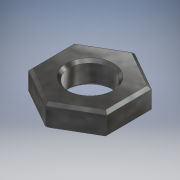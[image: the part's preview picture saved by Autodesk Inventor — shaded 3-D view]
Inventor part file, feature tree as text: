
AUTODESK INVENTOR PART (.ipt)
format: ipt  version: 2017 (Build 210142000, 142)  size: 131,072 bytes
history: native  units: mm
features: extrude x1, chamfer x1, sketch x1
ambient origin geometry x8: Origin, YZ Plane, XZ Plane, XY Plane, X Axis, Y Axis, Z Axis, Center Point
bodies: Solid1 (feature_tree)
feature tree (3):
  extrude  "Extrusion1"  Depth=5.0mm
  chamfer  "Chamfer1"  Distance=5.0mm
  sketch  "Sketch1"  dims[d0=9.02mm d1=8.5mm d2=5.0mm d3=0.0mm d4=0.6mm d5=2.0mm d6=45.0deg]
